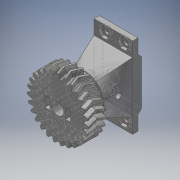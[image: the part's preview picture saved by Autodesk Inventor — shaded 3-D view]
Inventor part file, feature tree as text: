
AUTODESK INVENTOR PART (.ipt)
format: ipt  version: 2019 (Build 230136000, 136)  size: 1,001,472 bytes
history: native  units: mm (DEFAULTED — no unit token found)
features: sketch x23, extrude x15, plane x9, hole x6, other x4, mirror x4, chamfer x4, loft x1
ambient origin geometry x8: Origin, YZ Plane, XZ Plane, XY Plane, X Axis, Y Axis, Z Axis, Center Point
bodies: Solid1 (feature_tree)
feature tree (66):
  extrude  "Extrusion1"  Depth=5.0mm TaperAngle=0.0deg
  plane  "Work Plane2"
  plane  "Work Plane8"
  plane  "Work Plane9"
  other  "Spur Gear"
  mirror  "Mirror1"
  plane  "Work Plane11"
  extrude  "Extrusion2"  Depth=10.0mm TaperAngle=0.0deg
  extrude  "Extrusion3"  Depth=1.163553mm TaperAngle=0.0deg
  chamfer  "Chamfer1"  [1 undecoded]
  hole  "Hole1"  [1 undecoded]
  hole  "Hole2"  [1 undecoded]
  extrude  "Extrusion4"  Depth=3.75mm TaperAngle=45.0deg
  plane  "Work Plane13"
  extrude  "Extrusion5"  Depth=10.0mm
  plane  "Work Plane14"
  hole  "Hole3"  [1 undecoded]
  plane  "Work Plane15"
  hole  "Hole4"  [1 undecoded]
  extrude  "Extrusion6"  Depth=10.0mm
  extrude  "Extrusion7"  [1 undecoded]
  chamfer  "Chamfer2"  Distance=8.0mm
  extrude  "Extrusion9"  Depth=0.75mm TaperAngle=45.0deg
  extrude  "Extrusion10"  Depth=45.1mm
  chamfer  "Chamfer4"  Distance=5.0mm
  extrude  "Extrusion11"  Depth=10.0mm
  hole  "Hole5"  [1 undecoded]
  extrude  "Extrusion12"  Depth=10.0mm TaperAngle=0.0deg
  mirror  "Mirror2"
  plane  "Work Plane16"
  extrude  "Extrusion13"  Depth=10.0mm
  mirror  "Mirror3"
  chamfer  "Chamfer6"  Distance=5.5mm
  extrude  "Extrusion14"  Depth=10.0mm TaperAngle=0.0deg
  loft  "Loft1"
  extrude  "Extrusion15"  Depth=10.0mm TaperAngle=0.0deg
  plane  "Work Plane17"
  extrude  "Extrusion16"  Depth=10.0mm TaperAngle=45.0deg
  hole  "Hole6"  [1 undecoded]
  mirror  "Mirror4"
  sketch  "Sketch1"  dims[d0=34.130032mm d1=5.0mm d2=0.0mm]
  sketch  "Sketch2"  dims[d3=31.880377mm d4=10.0mm d5=0.0mm]
  other  "Srf1"
  sketch  "Sketch6"  dims[d16=31.29mm d17=0.0mm d34=1.163553mm]
  sketch  "Sketch7"  dims[d39=0.0mm]
  sketch  "Sketch9"  dims[d41=0.0mm]
  sketch  "Sketch10"  dims[d43=31.29mm]
  sketch  "Sketch11"  dims[d46=31.29mm d47=0.0mm d48=0.0mm]
  sketch  "Sketch12"  dims[d49=5.0mm d52=29.0mm]
  sketch  "Sketch13"  dims[d53=20.0mm d54=0.0mm d55=20.0mm]
  sketch  "Sketch14"  dims[d56=15.0mm d57=0.0mm d58=3.75mm d59=2.0mm d60=45.0deg]
  sketch  "Sketch15"  dims[d61=7.5mm d62=6.0mm d63=4.0mm d64=2.0mm d65=90.0deg d66=8.0mm d67=20.594885mm]
  sketch  "Sketch16"  dims[d68=6.5mm d69=6.0mm d70=4.0mm d71=2.0mm d72=90.0deg d73=8.0mm d74=0.0mm d75=10.0mm]
  sketch  "Sketch18"  dims[d76=1.0mm d77=10.0mm d78=0.0mm]
  sketch  "Sketch19"  dims[d79=10.0mm d80=1.0mm]
  sketch  "Sketch20"  dims[d81=20.0mm d82=0.0mm d83=10.0mm]
  sketch  "Sketch21"  dims[d84=3.5mm]
  sketch  "Sketch22"  dims[d85=3.5mm d86=6.0mm d87=6.0mm d88=7.0mm d89=90.0deg d90=8.0mm d91=0.0mm d92=-10.0mm]
  sketch  "Sketch23"  dims[d93=3.5mm d94=6.0mm d95=4.0mm d96=5.0mm d97=90.0deg d98=8.0mm d99=0.0mm]
  sketch  "Sketch24"  dims[d100=5.5mm d101=8.0mm d102=0.0mm]
  sketch  "Sketch26"  dims[d103=1.0mm d104=0.0mm d110=0.75mm d111=2.0mm d112=45.0deg]
  other  "Edges1"
  sketch  "Sketch27"  dims[d116=21.5mm d117=45.1mm d118=5.0mm d119=0.0mm]
  sketch  "Sketch28"  dims[d120=10.0mm d121=10.0mm]
  sketch  "Sketch29"  dims[d122=2.0mm d123=0.0mm d124=2.0mm d125=2.0mm d126=45.0deg d127=2.0mm d128=0.0mm d132=3.5mm d133=6.0mm d134=4.0mm d135=5.0mm d136=90.0deg d137=8.0mm d138=0.0mm d139=5.5mm d140=5.5mm d141=1.75mm d142=0.0mm d143=10.0mm d144=1.75mm d145=0.0mm d146=4.5mm d147=2.0mm d148=45.0deg d149=10.0mm d150=0.0mm d151=21.5mm d152=0.0mm d153=90.0deg d154=0.0mm d155=90.0deg d156=6.65mm d157=31.0mm d158=0.0mm d159=-5.0mm d160=5.9mm d161=2.7mm d162=0.0mm d163=3.1mm d164=6.0mm d165=6.5mm d166=7.5mm d167=90.0deg d168=10.0mm d169=0.0mm]
  other  "Pitch Diameter"
note: 8 required parameter values undecoded (feature->parameter linkage not recoverable at this tier; creation-order binding heuristic only, values carry confidence <= 0.55)
